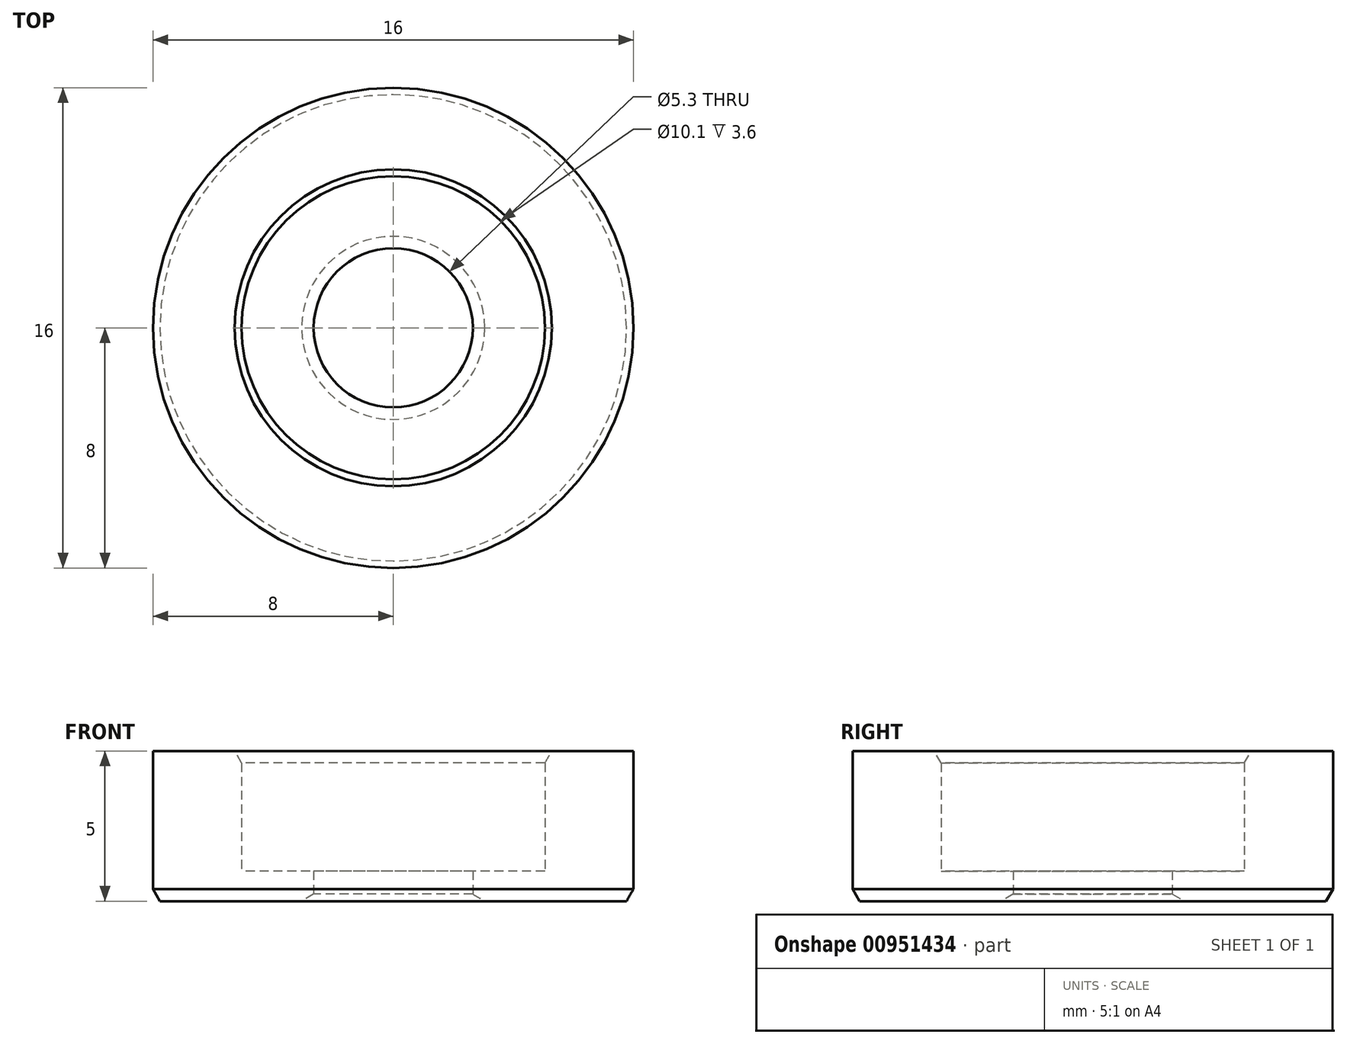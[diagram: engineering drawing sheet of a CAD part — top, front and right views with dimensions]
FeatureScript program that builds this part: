
annotation { "Feature Type Name" : "Feature", "Feature Type Description" : "" }
export const myFeature = defineFeature(function(context is Context, id is Id, definition is map)
    precondition{}
    {
        {
            var Q0;
            Q0=qCreatedBy(makeId("Top.planeOp"),FACE);
            var sketch = newSketch(context, id + "F0", { "sketchPlane" : qUnion([Q0])});
            skCircle(sketch, "E0", {"center": v(0, 0) * mm, "radius": 5.05 * mm});
            skCircle(sketch, "E1", {"center": v(0, 0) * mm, "radius": 8 * mm});
            skCircle(sketch, "E2", {"center": v(0, 0) * mm, "radius": 2.65 * mm});
            skSolve(sketch);
        }
        {
            var Q0;
            Q0=makeQuery(id+"F0.imprint","IMPRINT",FACE,{"disambiguationData":[TD([[makeQuery(id+"F0.imprint","IMPRINT",EDGE,{"derivedFrom":sQuery(id+"F0.wireOp",EDGE,"E0")}),1.0]])]});
            extrude(context, id + "F1", {"entities" : qUnion([Q0]), "depth" : 1 * mm, "offsetDistance" : 25 * mm});
        }
        {
            var Q0;
            Q0=makeQuery(id+"F0.imprint","IMPRINT",FACE,{"disambiguationData":[TD([[makeQuery(id+"F0.imprint","IMPRINT",EDGE,{"derivedFrom":sQuery(id+"F0.wireOp",EDGE,"E0")}),-1.0]])]});
            extrude(context, id + "F2", {"entities" : qUnion([Q0]), "operationType" : NewBodyOperationType.ADD, "depth" : 5 * mm, "offsetDistance" : 25 * mm});
        }
        {
            var Q0;
            Q0=makeQuery(id+"F2.opExtrude","CAP_EDGE",EDGE,{"disambiguationData":[OSD([sQuery(id+"F0.wireOp",EDGE,"E0")])],"isStart":false});
            var Q1;
            Q1=makeQuery(id+"F2.opExtrude","CAP_EDGE",EDGE,{"disambiguationData":[OSD([sQuery(id+"F0.wireOp",EDGE,"E1")])],"isStart":true});
            var Q2;
            Q2=makeQuery(id+"F1.opExtrude","CAP_EDGE",EDGE,{"disambiguationData":[OSD([sQuery(id+"F0.wireOp",EDGE,"E2")])],"isStart":true});
            chamfer(context, id + "F3", {"entities" : qUnion([Q0, Q1, Q2]), "chamferType" : ChamferType.OFFSET_ANGLE, "width" : 0.4 * mm, "oppositeDirection" : false, "angle" : 30 * degree, "tangentPropagation" : true});
        }
    });
